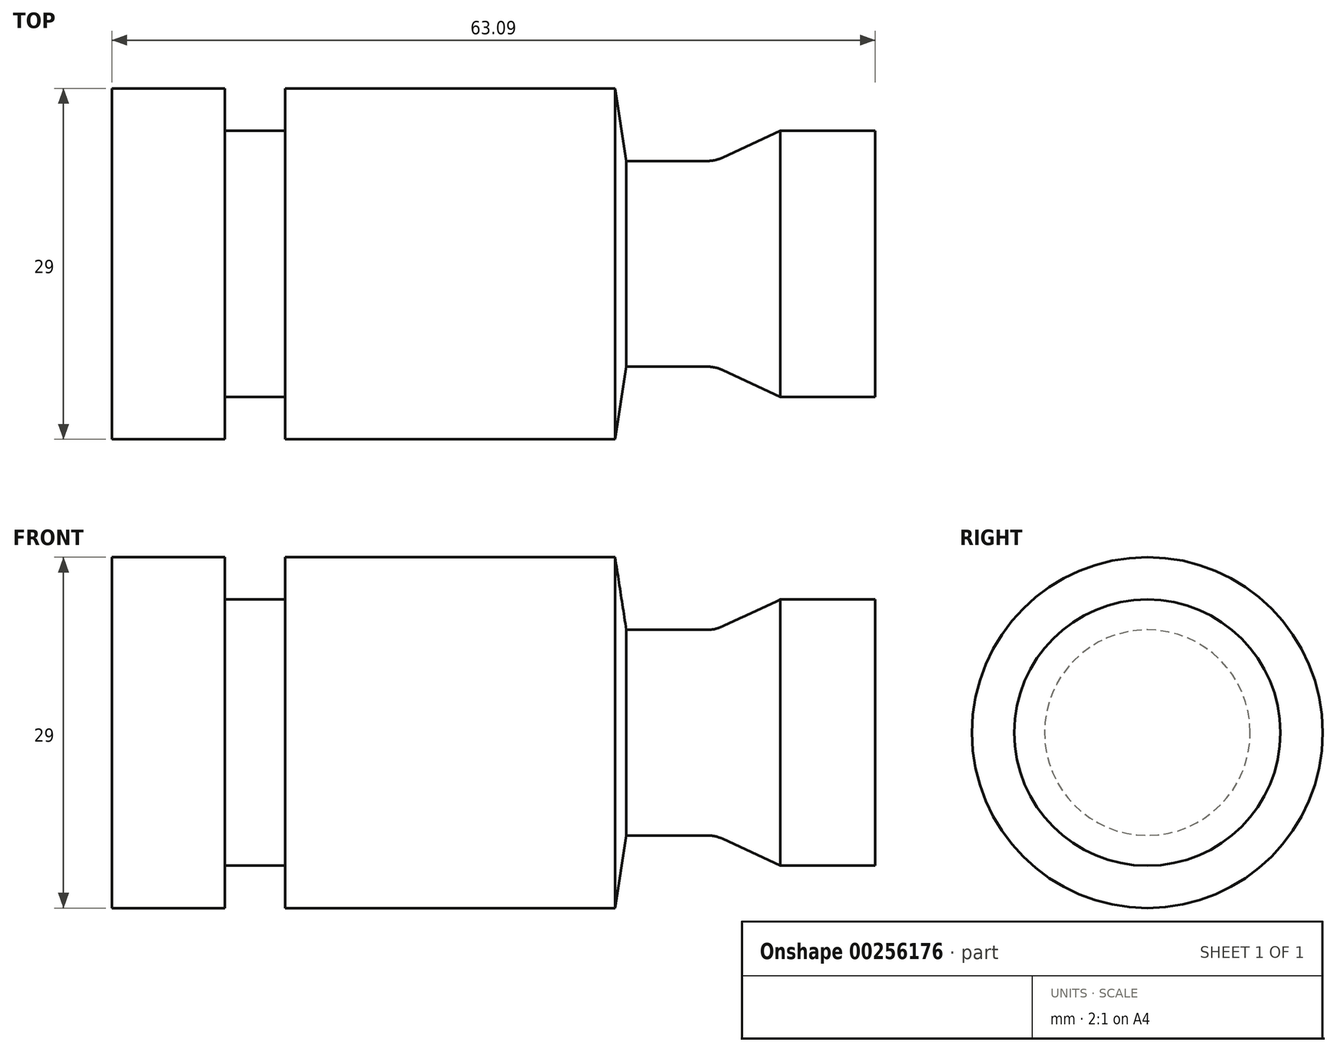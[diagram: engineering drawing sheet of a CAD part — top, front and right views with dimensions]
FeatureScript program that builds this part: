
annotation { "Feature Type Name" : "Feature", "Feature Type Description" : "" }
export const myFeature = defineFeature(function(context is Context, id is Id, definition is map)
    precondition{}
    {
        {
            var Q0;
            Q0=qCreatedBy(makeId("Front.planeOp"),FACE);
            var sketch = newSketch(context, id + "F0", { "sketchPlane" : qUnion([Q0])});
            skLineSegment(sketch, "E0", {"start": v(0, 11) * mm, "end": v(-7.85, 11) * mm});
            skLineSegment(sketch, "E1", {"start": v(-7.85, 11) * mm, "end": v(-12.6, 8.78) * mm});
            skLineSegment(sketch, "E2", {"start": v(-13.88, 8.5) * mm, "end": v(-20.57, 8.5) * mm});
            skLineSegment(sketch, "E3", {"start": v(-30.57, 14.5) * mm, "end": v(-38.35, 19.17) * mm});
            skLineSegment(sketch, "E4", {"start": v(-21.5, 14.5) * mm, "end": v(-48.77, 14.5) * mm});
            skLineSegment(sketch, "E5", {"start": v(-48.77, 14.5) * mm, "end": v(-48.77, 11) * mm});
            skLineSegment(sketch, "E6", {"start": v(-48.77, 11) * mm, "end": v(-53.75, 11) * mm});
            skLineSegment(sketch, "E7", {"start": v(-53.75, 11) * mm, "end": v(-53.75, 14.5) * mm});
            skLineSegment(sketch, "E8", {"start": v(-53.75, 14.5) * mm, "end": v(-63.1, 14.5) * mm});
            skLineSegment(sketch, "E9", {"start": v(-63.1, 14.5) * mm, "end": v(-63.1, 0) * mm});
            skLineSegment(sketch, "E10", {"start": v(-63.1, 0) * mm, "end": v(0, 0) * mm});
            skLineSegment(sketch, "E11", {"start": v(0, 0) * mm, "end": v(0, 11) * mm});
            skArc(sketch, "E12", {"start": v(-13.88, 8.5) * mm, "mid": v(-13.23, 8.57) * mm, "end": v(-12.6, 8.78) * mm});
            skPoint(sketch, "E13.orphan", {"position": v(-13.21, 8.5) * mm});
            skLineSegment(sketch, "E14", {"start": v(-20.57, 8.5) * mm, "end": v(-21.5, 14.5) * mm});
            skSolve(sketch);
        }
        {
            var Q0;
            Q0=makeQuery(id+"F0.imprint","IMPRINT",FACE,{"disambiguationData":[TD([[makeQuery(id+"F0.imprint","IMPRINT",EDGE,{"derivedFrom":sQuery(id+"F0.wireOp",EDGE,"E0")}),1.0]])]});
            var Q1;
            Q1=sQuery(id+"F0.wireOp",EDGE,"E10");
            revolve(context, id + "F1", {"entities" : qUnion([Q0]), "axis" : qUnion([Q1]), "revolveType" : RevolveType.FULL});
        }
        {
            var Q0;
            Q0=makeQuery(id+"F1.opRevolve","SWEPT_FACE",FACE,{"disambiguationData":[OSD([sQuery(id+"F0.wireOp",EDGE,"E11")])]});
            var sketch = newSketch(context, id + "F2", { "sketchPlane" : qUnion([Q0])});
            skCircle(sketch, "E15", {"center": v(0, 0) * mm, "radius": 6 * mm});
            skSolve(sketch);
        }
        {
            var Q0;
            Q0=makeQuery(id+"F2.imprint","IMPRINT",FACE,{"disambiguationData":[TD([[makeQuery(id+"F2.imprint","IMPRINT",EDGE,{"derivedFrom":sQuery(id+"F2.wireOp",EDGE,"E15")}),1.0]])]});
            extrude(context, id + "F3", {"entities" : qUnion([Q0]), "operationType" : NewBodyOperationType.ADD, "oppositeDirection" : true, "depth" : 25 * mm});
        }
    });
